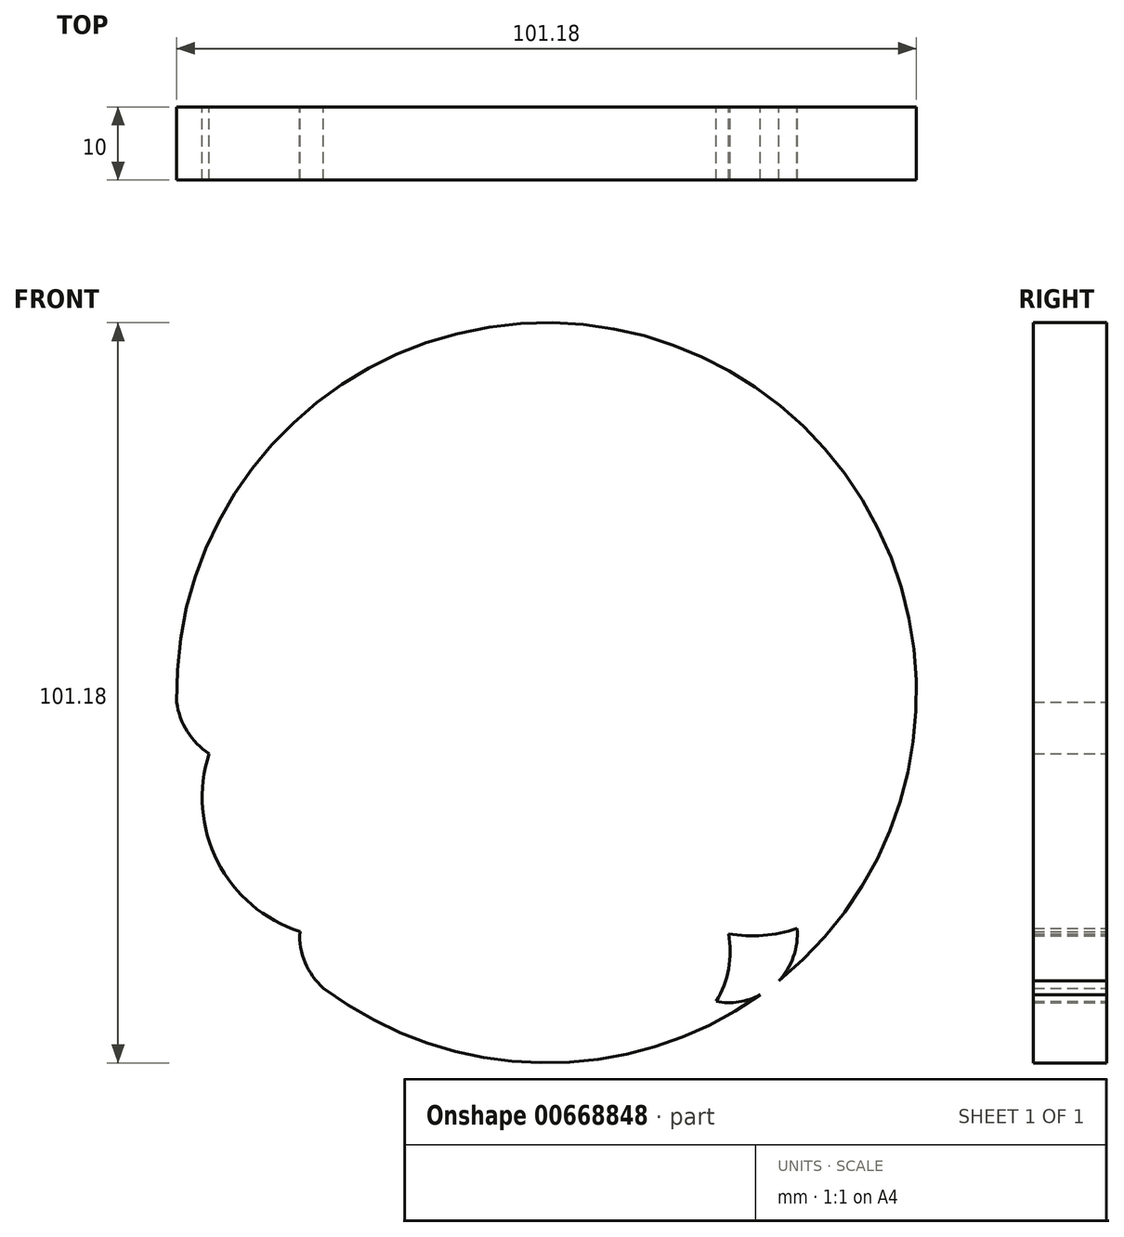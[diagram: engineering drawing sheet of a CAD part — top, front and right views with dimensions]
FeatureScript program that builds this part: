
annotation { "Feature Type Name" : "Feature", "Feature Type Description" : "" }
export const myFeature = defineFeature(function(context is Context, id is Id, definition is map)
    precondition{}
    {
        {
            var Q0;
            Q0=qCreatedBy(makeId("Front.planeOp"),FACE);
            var sketch = newSketch(context, id + "F0", { "sketchPlane" : qUnion([Q0])});
            skCircle(sketch, "E0", {"center": v(0, 0) * mm, "radius": 12.41 * mm});
            skCircle(sketch, "E1", {"center": v(0, 0) * mm, "radius": 50.59 * mm});
            skCircle(sketch, "E2", {"center": v(-26.62, 32.1) * mm, "radius": 8.89 * mm});
            skCircle(sketch, "E3", {"center": v(0, 41.3) * mm, "radius": 8.95 * mm});
            skCircle(sketch, "E4", {"center": v(27.2, 30.94) * mm, "radius": 9.28 * mm});
            skCircle(sketch, "E5", {"center": v(41.01, 0) * mm, "radius": 9.53 * mm});
            skCircle(sketch, "E6", {"center": v(-40.72, 0) * mm, "radius": 9.93 * mm});
            skCircle(sketch, "E7", {"center": v(0, -40.72) * mm, "radius": 9.22 * mm});
            skCircle(sketch, "E8", {"center": v(-24.32, -33.24) * mm, "radius": 9.43 * mm});
            skCircle(sketch, "E9", {"center": v(24.9, -32.95) * mm, "radius": 9.4 * mm});
            skLineSegment(sketch, "E10", {"start": v(0, 0) * mm, "end": v(0, 41.3) * mm});
            skLineSegment(sketch, "E11", {"start": v(0, 0) * mm, "end": v(27.2, 30.94) * mm});
            skLineSegment(sketch, "E12", {"start": v(0, 0) * mm, "end": v(41.01, 0) * mm});
            skLineSegment(sketch, "E13", {"start": v(0, 0) * mm, "end": v(24.9, -32.95) * mm});
            skLineSegment(sketch, "E14", {"start": v(0, 0) * mm, "end": v(0, -40.72) * mm});
            skLineSegment(sketch, "E15", {"start": v(0, 0) * mm, "end": v(-24.32, -33.24) * mm});
            skLineSegment(sketch, "E16", {"start": v(0, 0) * mm, "end": v(-40.72, 0) * mm});
            skLineSegment(sketch, "E17", {"start": v(0, 0) * mm, "end": v(-26.62, 32.1) * mm});
            skArc(sketch, "E18", {"start": v(-26.62, 32.1) * mm, "mid": v(-45.76, 21.36) * mm, "end": v(-40.72, 0) * mm});
            skArc(sketch, "E19", {"start": v(-40.72, 0) * mm, "mid": v(-45.1, -22.83) * mm, "end": v(-24.32, -33.24) * mm});
            skArc(sketch, "E20", {"start": v(-24.32, -33.24) * mm, "mid": v(-15.57, -48.07) * mm, "end": v(0, -40.72) * mm});
            skArc(sketch, "E21", {"start": v(0, -40.72) * mm, "mid": v(15.9, -47.9) * mm, "end": v(24.9, -32.95) * mm});
            skArc(sketch, "E22", {"start": v(24.9, -32.95) * mm, "mid": v(45.28, -22.5) * mm, "end": v(41.01, 0) * mm});
            skArc(sketch, "E23", {"start": v(41.01, 0) * mm, "mid": v(45.96, 20.76) * mm, "end": v(27.2, 30.94) * mm});
            skArc(sketch, "E24", {"start": v(27.2, 30.94) * mm, "mid": v(17.84, 47.26) * mm, "end": v(0, 41.3) * mm});
            skArc(sketch, "E25", {"start": v(0, 41.3) * mm, "mid": v(-17, 47.35) * mm, "end": v(-26.62, 32.1) * mm});
            skLineSegment(sketch, "E26", {"start": v(-29.07, 14.02) * mm, "end": v(-40.72, 0) * mm});
            skLineSegment(sketch, "E27", {"start": v(-29.07, 14.02) * mm, "end": v(-26.62, 32.1) * mm});
            skLineSegment(sketch, "E28", {"start": v(-12.28, 33.71) * mm, "end": v(-26.62, 32.1) * mm});
            skLineSegment(sketch, "E29", {"start": v(-12.28, 33.71) * mm, "end": v(0, 41.3) * mm});
            skLineSegment(sketch, "E30", {"start": v(0, 41.3) * mm, "end": v(12.56, 33.4) * mm});
            skLineSegment(sketch, "E31", {"start": v(12.56, 33.4) * mm, "end": v(27.2, 30.94) * mm});
            skLineSegment(sketch, "E32", {"start": v(27.2, 30.94) * mm, "end": v(29.94, 13.61) * mm});
            skLineSegment(sketch, "E33", {"start": v(29.94, 13.61) * mm, "end": v(41.01, 0) * mm});
            skLineSegment(sketch, "E34", {"start": v(41.01, 0) * mm, "end": v(28.11, -14.1) * mm});
            skLineSegment(sketch, "E35", {"start": v(28.11, -14.1) * mm, "end": v(24.9, -32.95) * mm});
            skLineSegment(sketch, "E36", {"start": v(24.9, -32.95) * mm, "end": v(11.99, -35.37) * mm});
            skLineSegment(sketch, "E37", {"start": v(11.99, -35.37) * mm, "end": v(0, -40.72) * mm});
            skLineSegment(sketch, "E38", {"start": v(0, -40.72) * mm, "end": v(-11.81, -35.85) * mm});
            skLineSegment(sketch, "E39", {"start": v(-11.81, -35.85) * mm, "end": v(-24.32, -33.24) * mm});
            skLineSegment(sketch, "E40", {"start": v(-24.32, -33.24) * mm, "end": v(-27.83, -14.3) * mm});
            skLineSegment(sketch, "E41", {"start": v(-27.83, -14.3) * mm, "end": v(-40.72, 0) * mm});
            skSolve(sketch);
        }
        {
            var Q0;
            {var subQ3=sQuery(id+"F0.wireOp",EDGE,"E11");var subQ10=sQuery(id+"F0.wireOp",EDGE,"E0");var subQ12=makeQuery(id+"F0.imprint","INTERSECT",VERTEX,{"derivedFrom":[subQ10,subQ3]});Q0=makeQuery(id+"F0.imprint","IMPRINT",FACE,{"disambiguationData":[TD([[makeQuery(id+"F0.imprint","IMPRINT",EDGE,{"disambiguationData":[TD([[subQ12,-1.0]])],"derivedFrom":subQ10}),-1.0]])]});}
            var Q1;
            {var subQ0=sQuery(id+"F0.wireOp",EDGE,"E10");var subQ1=sQuery(id+"F0.wireOp",EDGE,"E0");var subQ2=makeQuery(id+"F0.imprint","INTERSECT",VERTEX,{"derivedFrom":[subQ1,subQ0]});Q1=makeQuery(id+"F0.imprint","IMPRINT",FACE,{"disambiguationData":[TD([[makeQuery(id+"F0.imprint","IMPRINT",EDGE,{"disambiguationData":[TD([[subQ2,-1.0]])],"derivedFrom":subQ1}),-1.0]])]});}
            var Q2;
            {var subQ3=sQuery(id+"F0.wireOp",EDGE,"E2");var subQ5=sQuery(id+"F0.wireOp",EDGE,"E25");var subQ6=makeQuery(id+"F0.imprint","INTERSECT",VERTEX,{"derivedFrom":[subQ3,subQ5]});Q2=makeQuery(id+"F0.imprint","IMPRINT",FACE,{"disambiguationData":[TD([[makeQuery(id+"F0.imprint","IMPRINT",EDGE,{"disambiguationData":[TD([[subQ6,1.0]])],"derivedFrom":subQ3}),-1.0]])]});}
            var Q3;
            {var subQ0=sQuery(id+"F0.wireOp",EDGE,"E25");var subQ1=sQuery(id+"F0.wireOp",EDGE,"E3");var subQ2=makeQuery(id+"F0.imprint","INTERSECT",VERTEX,{"derivedFrom":[subQ1,subQ0]});Q3=makeQuery(id+"F0.imprint","IMPRINT",FACE,{"disambiguationData":[TD([[makeQuery(id+"F0.imprint","IMPRINT",EDGE,{"disambiguationData":[TD([[subQ2,-1.0]])],"derivedFrom":subQ1}),1.0]])]});}
            var Q4;
            {var subQ0=sQuery(id+"F0.wireOp",EDGE,"E25");var subQ1=sQuery(id+"F0.wireOp",EDGE,"E3");var subQ2=makeQuery(id+"F0.imprint","INTERSECT",VERTEX,{"derivedFrom":[subQ1,subQ0]});Q4=makeQuery(id+"F0.imprint","IMPRINT",FACE,{"disambiguationData":[TD([[makeQuery(id+"F0.imprint","IMPRINT",EDGE,{"disambiguationData":[TD([[subQ2,1.0]])],"derivedFrom":subQ1}),1.0]])]});}
            var Q5;
            {var subQ0=sQuery(id+"F0.wireOp",EDGE,"E24");var subQ1=sQuery(id+"F0.wireOp",EDGE,"E3");var subQ2=makeQuery(id+"F0.imprint","INTERSECT",VERTEX,{"derivedFrom":[subQ1,subQ0]});Q5=makeQuery(id+"F0.imprint","IMPRINT",FACE,{"disambiguationData":[TD([[makeQuery(id+"F0.imprint","IMPRINT",EDGE,{"disambiguationData":[TD([[subQ2,1.0]])],"derivedFrom":subQ1}),1.0]])]});}
            var Q6;
            {var subQ0=sQuery(id+"F0.wireOp",EDGE,"E10");var subQ1=sQuery(id+"F0.wireOp",EDGE,"E3");var subQ2=makeQuery(id+"F0.imprint","INTERSECT",VERTEX,{"derivedFrom":[subQ1,subQ0]});Q6=makeQuery(id+"F0.imprint","IMPRINT",FACE,{"disambiguationData":[TD([[makeQuery(id+"F0.imprint","IMPRINT",EDGE,{"disambiguationData":[TD([[subQ2,-1.0]])],"derivedFrom":subQ1}),1.0]])]});}
            var Q7;
            {var subQ0=sQuery(id+"F0.wireOp",EDGE,"E29");var subQ1=sQuery(id+"F0.wireOp",EDGE,"E3");var subQ2=makeQuery(id+"F0.imprint","INTERSECT",VERTEX,{"derivedFrom":[subQ1,subQ0]});Q7=makeQuery(id+"F0.imprint","IMPRINT",FACE,{"disambiguationData":[TD([[makeQuery(id+"F0.imprint","IMPRINT",EDGE,{"disambiguationData":[TD([[subQ2,-1.0]])],"derivedFrom":subQ1}),1.0]])]});}
            var Q8;
            {var subQ11=sQuery(id+"F0.wireOp",EDGE,"E6");var subQ12=sQuery(id+"F0.wireOp",EDGE,"E1");var subQ13=makeQuery(id+"F0.imprint","INTERSECT",VERTEX,{"disambiguationData":[OD(1.0)],"derivedFrom":[subQ12,subQ11]});Q8=makeQuery(id+"F0.imprint","IMPRINT",FACE,{"disambiguationData":[TD([[makeQuery(id+"F0.imprint","IMPRINT",EDGE,{"disambiguationData":[TD([[subQ13,1.0]])],"derivedFrom":subQ12}),1.0]])]});}
            var Q9;
            {var subQ5=sQuery(id+"F0.wireOp",EDGE,"E18");var subQ6=sQuery(id+"F0.wireOp",EDGE,"E2");var subQ7=makeQuery(id+"F0.imprint","INTERSECT",VERTEX,{"derivedFrom":[subQ6,subQ5]});Q9=makeQuery(id+"F0.imprint","IMPRINT",FACE,{"disambiguationData":[TD([[makeQuery(id+"F0.imprint","IMPRINT",EDGE,{"disambiguationData":[TD([[subQ7,-1.0]])],"derivedFrom":subQ6}),-1.0]])]});}
            var Q10;
            {var subQ0=sQuery(id+"F0.wireOp",EDGE,"E18");var subQ1=sQuery(id+"F0.wireOp",EDGE,"E2");var subQ2=makeQuery(id+"F0.imprint","INTERSECT",VERTEX,{"derivedFrom":[subQ1,subQ0]});Q10=makeQuery(id+"F0.imprint","IMPRINT",FACE,{"disambiguationData":[TD([[makeQuery(id+"F0.imprint","IMPRINT",EDGE,{"disambiguationData":[TD([[subQ2,-1.0]])],"derivedFrom":subQ1}),1.0]])]});}
            var Q11;
            {var subQ0=sQuery(id+"F0.wireOp",EDGE,"E25");var subQ1=sQuery(id+"F0.wireOp",EDGE,"E2");var subQ2=makeQuery(id+"F0.imprint","INTERSECT",VERTEX,{"derivedFrom":[subQ1,subQ0]});Q11=makeQuery(id+"F0.imprint","IMPRINT",FACE,{"disambiguationData":[TD([[makeQuery(id+"F0.imprint","IMPRINT",EDGE,{"disambiguationData":[TD([[subQ2,-1.0]])],"derivedFrom":subQ1}),1.0]])]});}
            var Q12;
            {var subQ0=sQuery(id+"F0.wireOp",EDGE,"E25");var subQ1=sQuery(id+"F0.wireOp",EDGE,"E2");var subQ2=makeQuery(id+"F0.imprint","INTERSECT",VERTEX,{"derivedFrom":[subQ1,subQ0]});Q12=makeQuery(id+"F0.imprint","IMPRINT",FACE,{"disambiguationData":[TD([[makeQuery(id+"F0.imprint","IMPRINT",EDGE,{"disambiguationData":[TD([[subQ2,1.0]])],"derivedFrom":subQ1}),1.0]])]});}
            var Q13;
            {var subQ0=sQuery(id+"F0.wireOp",EDGE,"E28");var subQ1=sQuery(id+"F0.wireOp",EDGE,"E2");var subQ2=makeQuery(id+"F0.imprint","INTERSECT",VERTEX,{"derivedFrom":[subQ1,subQ0]});Q13=makeQuery(id+"F0.imprint","IMPRINT",FACE,{"disambiguationData":[TD([[makeQuery(id+"F0.imprint","IMPRINT",EDGE,{"disambiguationData":[TD([[subQ2,1.0]])],"derivedFrom":subQ1}),1.0]])]});}
            var Q14;
            {var subQ0=sQuery(id+"F0.wireOp",EDGE,"E27");var subQ1=sQuery(id+"F0.wireOp",EDGE,"E2");var subQ2=makeQuery(id+"F0.imprint","INTERSECT",VERTEX,{"derivedFrom":[subQ1,subQ0]});Q14=makeQuery(id+"F0.imprint","IMPRINT",FACE,{"disambiguationData":[TD([[makeQuery(id+"F0.imprint","IMPRINT",EDGE,{"disambiguationData":[TD([[subQ2,-1.0]])],"derivedFrom":subQ1}),1.0]])]});}
            var Q15;
            {var subQ1=sQuery(id+"F0.wireOp",EDGE,"E0");var subQ10=sQuery(id+"F0.wireOp",EDGE,"E17");var subQ12=makeQuery(id+"F0.imprint","INTERSECT",VERTEX,{"derivedFrom":[subQ1,subQ10]});Q15=makeQuery(id+"F0.imprint","IMPRINT",FACE,{"disambiguationData":[TD([[makeQuery(id+"F0.imprint","IMPRINT",EDGE,{"disambiguationData":[TD([[subQ12,-1.0]])],"derivedFrom":subQ1}),-1.0]])]});}
            var Q16;
            {var subQ0=sQuery(id+"F0.wireOp",EDGE,"E16");var subQ1=sQuery(id+"F0.wireOp",EDGE,"E6");var subQ2=makeQuery(id+"F0.imprint","INTERSECT",VERTEX,{"derivedFrom":[subQ1,subQ0]});Q16=makeQuery(id+"F0.imprint","IMPRINT",FACE,{"disambiguationData":[TD([[makeQuery(id+"F0.imprint","IMPRINT",EDGE,{"disambiguationData":[TD([[subQ2,1.0]])],"derivedFrom":subQ1}),1.0]])]});}
            var Q17;
            {var subQ0=sQuery(id+"F0.wireOp",EDGE,"E26");var subQ1=sQuery(id+"F0.wireOp",EDGE,"E6");var subQ2=makeQuery(id+"F0.imprint","INTERSECT",VERTEX,{"derivedFrom":[subQ1,subQ0]});Q17=makeQuery(id+"F0.imprint","IMPRINT",FACE,{"disambiguationData":[TD([[makeQuery(id+"F0.imprint","IMPRINT",EDGE,{"disambiguationData":[TD([[subQ2,1.0]])],"derivedFrom":subQ1}),1.0]])]});}
            var Q18;
            {var subQ0=sQuery(id+"F0.wireOp",EDGE,"E26");var subQ1=sQuery(id+"F0.wireOp",EDGE,"E6");var subQ2=makeQuery(id+"F0.imprint","INTERSECT",VERTEX,{"derivedFrom":[subQ1,subQ0]});Q18=makeQuery(id+"F0.imprint","IMPRINT",FACE,{"disambiguationData":[TD([[makeQuery(id+"F0.imprint","IMPRINT",EDGE,{"disambiguationData":[TD([[subQ2,-1.0]])],"derivedFrom":subQ1}),1.0]])]});}
            var Q19;
            {var subQ3=sQuery(id+"F0.wireOp",EDGE,"E6");var subQ5=sQuery(id+"F0.wireOp",EDGE,"E1");var subQ7=makeQuery(id+"F0.imprint","INTERSECT",VERTEX,{"disambiguationData":[OD(0.0)],"derivedFrom":[subQ5,subQ3]});Q19=makeQuery(id+"F0.imprint","IMPRINT",FACE,{"disambiguationData":[TD([[makeQuery(id+"F0.imprint","IMPRINT",EDGE,{"disambiguationData":[TD([[subQ7,1.0]])],"derivedFrom":subQ5}),1.0]])]});}
            var Q20;
            {var subQ3=sQuery(id+"F0.wireOp",EDGE,"E6");var subQ5=sQuery(id+"F0.wireOp",EDGE,"E1");var subQ7=makeQuery(id+"F0.imprint","INTERSECT",VERTEX,{"disambiguationData":[OD(0.0)],"derivedFrom":[subQ5,subQ3]});Q20=makeQuery(id+"F0.imprint","IMPRINT",FACE,{"disambiguationData":[TD([[makeQuery(id+"F0.imprint","IMPRINT",EDGE,{"disambiguationData":[TD([[subQ7,1.0]])],"derivedFrom":subQ5}),1.0]])]});}
            var Q21;
            {var subQ0=sQuery(id+"F0.wireOp",EDGE,"E19");var subQ1=sQuery(id+"F0.wireOp",EDGE,"E6");var subQ2=makeQuery(id+"F0.imprint","INTERSECT",VERTEX,{"derivedFrom":[subQ1,subQ0]});Q21=makeQuery(id+"F0.imprint","IMPRINT",FACE,{"disambiguationData":[TD([[makeQuery(id+"F0.imprint","IMPRINT",EDGE,{"disambiguationData":[TD([[subQ2,-1.0]])],"derivedFrom":subQ1}),1.0]])]});}
            var Q22;
            {var subQ0=sQuery(id+"F0.wireOp",EDGE,"E6");var subQ1=sQuery(id+"F0.wireOp",EDGE,"E1");var subQ2=makeQuery(id+"F0.imprint","INTERSECT",VERTEX,{"disambiguationData":[OD(0.0)],"derivedFrom":[subQ1,subQ0]});Q22=makeQuery(id+"F0.imprint","IMPRINT",FACE,{"disambiguationData":[TD([[makeQuery(id+"F0.imprint","IMPRINT",EDGE,{"disambiguationData":[TD([[subQ2,-1.0]])],"derivedFrom":subQ1}),1.0]])]});}
            var Q23;
            {var subQ0=sQuery(id+"F0.wireOp",EDGE,"E19");var subQ1=sQuery(id+"F0.wireOp",EDGE,"E6");var subQ2=makeQuery(id+"F0.imprint","INTERSECT",VERTEX,{"derivedFrom":[subQ1,subQ0]});Q23=makeQuery(id+"F0.imprint","IMPRINT",FACE,{"disambiguationData":[TD([[makeQuery(id+"F0.imprint","IMPRINT",EDGE,{"disambiguationData":[TD([[subQ2,-1.0]])],"derivedFrom":subQ1}),-1.0]])]});}
            var Q24;
            {var subQ1=sQuery(id+"F0.wireOp",EDGE,"E0");var subQ7=sQuery(id+"F0.wireOp",EDGE,"E16");var subQ8=makeQuery(id+"F0.imprint","INTERSECT",VERTEX,{"derivedFrom":[subQ1,subQ7]});Q24=makeQuery(id+"F0.imprint","IMPRINT",FACE,{"disambiguationData":[TD([[makeQuery(id+"F0.imprint","IMPRINT",EDGE,{"disambiguationData":[TD([[subQ8,-1.0]])],"derivedFrom":subQ1}),-1.0]])]});}
            var Q25;
            {var subQ0=sQuery(id+"F0.wireOp",EDGE,"E40");var subQ1=sQuery(id+"F0.wireOp",EDGE,"E8");var subQ2=makeQuery(id+"F0.imprint","INTERSECT",VERTEX,{"derivedFrom":[subQ1,subQ0]});Q25=makeQuery(id+"F0.imprint","IMPRINT",FACE,{"disambiguationData":[TD([[makeQuery(id+"F0.imprint","IMPRINT",EDGE,{"disambiguationData":[TD([[subQ2,1.0]])],"derivedFrom":subQ1}),1.0]])]});}
            var Q26;
            {var subQ0=sQuery(id+"F0.wireOp",EDGE,"E40");var subQ1=sQuery(id+"F0.wireOp",EDGE,"E8");var subQ2=makeQuery(id+"F0.imprint","INTERSECT",VERTEX,{"derivedFrom":[subQ1,subQ0]});Q26=makeQuery(id+"F0.imprint","IMPRINT",FACE,{"disambiguationData":[TD([[makeQuery(id+"F0.imprint","IMPRINT",EDGE,{"disambiguationData":[TD([[subQ2,-1.0]])],"derivedFrom":subQ1}),1.0]])]});}
            var Q27;
            {var subQ3=sQuery(id+"F0.wireOp",EDGE,"E8");var subQ5=sQuery(id+"F0.wireOp",EDGE,"E1");var subQ6=makeQuery(id+"F0.imprint","INTERSECT",VERTEX,{"disambiguationData":[OD(0.0)],"derivedFrom":[subQ5,subQ3]});Q27=makeQuery(id+"F0.imprint","IMPRINT",FACE,{"disambiguationData":[TD([[makeQuery(id+"F0.imprint","IMPRINT",EDGE,{"disambiguationData":[TD([[subQ6,-1.0]])],"derivedFrom":subQ5}),1.0]])]});}
            var Q28;
            {var subQ0=sQuery(id+"F0.wireOp",EDGE,"E20");var subQ1=sQuery(id+"F0.wireOp",EDGE,"E8");var subQ2=makeQuery(id+"F0.imprint","INTERSECT",VERTEX,{"derivedFrom":[subQ1,subQ0]});Q28=makeQuery(id+"F0.imprint","IMPRINT",FACE,{"disambiguationData":[TD([[makeQuery(id+"F0.imprint","IMPRINT",EDGE,{"disambiguationData":[TD([[subQ2,-1.0]])],"derivedFrom":subQ1}),1.0]])]});}
            var Q29;
            {var subQ0=sQuery(id+"F0.wireOp",EDGE,"E15");var subQ1=sQuery(id+"F0.wireOp",EDGE,"E8");var subQ2=makeQuery(id+"F0.imprint","INTERSECT",VERTEX,{"derivedFrom":[subQ1,subQ0]});Q29=makeQuery(id+"F0.imprint","IMPRINT",FACE,{"disambiguationData":[TD([[makeQuery(id+"F0.imprint","IMPRINT",EDGE,{"disambiguationData":[TD([[subQ2,1.0]])],"derivedFrom":subQ1}),1.0]])]});}
            var Q30;
            {var subQ1=sQuery(id+"F0.wireOp",EDGE,"E0");var subQ5=sQuery(id+"F0.wireOp",EDGE,"E15");var subQ12=makeQuery(id+"F0.imprint","INTERSECT",VERTEX,{"derivedFrom":[subQ1,subQ5]});Q30=makeQuery(id+"F0.imprint","IMPRINT",FACE,{"disambiguationData":[TD([[makeQuery(id+"F0.imprint","IMPRINT",EDGE,{"disambiguationData":[TD([[subQ12,-1.0]])],"derivedFrom":subQ1}),-1.0]])]});}
            var Q31;
            {var subQ1=sQuery(id+"F0.wireOp",EDGE,"E7");var subQ7=sQuery(id+"F0.wireOp",EDGE,"E38");var subQ9=makeQuery(id+"F0.imprint","INTERSECT",VERTEX,{"derivedFrom":[subQ1,subQ7]});Q31=makeQuery(id+"F0.imprint","IMPRINT",FACE,{"disambiguationData":[TD([[makeQuery(id+"F0.imprint","IMPRINT",EDGE,{"disambiguationData":[TD([[subQ9,-1.0]])],"derivedFrom":subQ1}),-1.0]])]});}
            var Q32;
            {var subQ1=sQuery(id+"F0.wireOp",EDGE,"E1");var subQ5=sQuery(id+"F0.wireOp",EDGE,"E8");var subQ6=makeQuery(id+"F0.imprint","INTERSECT",VERTEX,{"disambiguationData":[OD(1.0)],"derivedFrom":[subQ1,subQ5]});Q32=makeQuery(id+"F0.imprint","IMPRINT",FACE,{"disambiguationData":[TD([[makeQuery(id+"F0.imprint","IMPRINT",EDGE,{"disambiguationData":[TD([[subQ6,-1.0]])],"derivedFrom":subQ1}),1.0]])]});}
            var Q33;
            {var subQ1=sQuery(id+"F0.wireOp",EDGE,"E0");var subQ7=sQuery(id+"F0.wireOp",EDGE,"E14");var subQ13=makeQuery(id+"F0.imprint","INTERSECT",VERTEX,{"derivedFrom":[subQ1,subQ7]});Q33=makeQuery(id+"F0.imprint","IMPRINT",FACE,{"disambiguationData":[TD([[makeQuery(id+"F0.imprint","IMPRINT",EDGE,{"disambiguationData":[TD([[subQ13,-1.0]])],"derivedFrom":subQ1}),-1.0]])]});}
            var Q34;
            {var subQ0=sQuery(id+"F0.wireOp",EDGE,"E37");var subQ6=sQuery(id+"F0.wireOp",EDGE,"E7");var subQ9=makeQuery(id+"F0.imprint","INTERSECT",VERTEX,{"derivedFrom":[subQ6,subQ0]});Q34=makeQuery(id+"F0.imprint","IMPRINT",FACE,{"disambiguationData":[TD([[makeQuery(id+"F0.imprint","IMPRINT",EDGE,{"disambiguationData":[TD([[subQ9,1.0]])],"derivedFrom":subQ6}),-1.0]])]});}
            var Q35;
            {var subQ0=sQuery(id+"F0.wireOp",EDGE,"E14");var subQ1=sQuery(id+"F0.wireOp",EDGE,"E7");var subQ2=makeQuery(id+"F0.imprint","INTERSECT",VERTEX,{"derivedFrom":[subQ1,subQ0]});Q35=makeQuery(id+"F0.imprint","IMPRINT",FACE,{"disambiguationData":[TD([[makeQuery(id+"F0.imprint","IMPRINT",EDGE,{"disambiguationData":[TD([[subQ2,1.0]])],"derivedFrom":subQ1}),1.0]])]});}
            var Q36;
            {var subQ0=sQuery(id+"F0.wireOp",EDGE,"E14");var subQ1=sQuery(id+"F0.wireOp",EDGE,"E7");var subQ2=makeQuery(id+"F0.imprint","INTERSECT",VERTEX,{"derivedFrom":[subQ1,subQ0]});Q36=makeQuery(id+"F0.imprint","IMPRINT",FACE,{"disambiguationData":[TD([[makeQuery(id+"F0.imprint","IMPRINT",EDGE,{"disambiguationData":[TD([[subQ2,-1.0]])],"derivedFrom":subQ1}),1.0]])]});}
            var Q37;
            {var subQ0=sQuery(id+"F0.wireOp",EDGE,"E38");var subQ1=sQuery(id+"F0.wireOp",EDGE,"E7");var subQ2=makeQuery(id+"F0.imprint","INTERSECT",VERTEX,{"derivedFrom":[subQ1,subQ0]});Q37=makeQuery(id+"F0.imprint","IMPRINT",FACE,{"disambiguationData":[TD([[makeQuery(id+"F0.imprint","IMPRINT",EDGE,{"disambiguationData":[TD([[subQ2,-1.0]])],"derivedFrom":subQ1}),1.0]])]});}
            var Q38;
            {var subQ0=sQuery(id+"F0.wireOp",EDGE,"E20");var subQ1=sQuery(id+"F0.wireOp",EDGE,"E7");var subQ2=makeQuery(id+"F0.imprint","INTERSECT",VERTEX,{"derivedFrom":[subQ1,subQ0]});Q38=makeQuery(id+"F0.imprint","IMPRINT",FACE,{"disambiguationData":[TD([[makeQuery(id+"F0.imprint","IMPRINT",EDGE,{"disambiguationData":[TD([[subQ2,-1.0]])],"derivedFrom":subQ1}),1.0]])]});}
            var Q39;
            {var subQ0=sQuery(id+"F0.wireOp",EDGE,"E37");var subQ1=sQuery(id+"F0.wireOp",EDGE,"E7");var subQ2=makeQuery(id+"F0.imprint","INTERSECT",VERTEX,{"derivedFrom":[subQ1,subQ0]});Q39=makeQuery(id+"F0.imprint","IMPRINT",FACE,{"disambiguationData":[TD([[makeQuery(id+"F0.imprint","IMPRINT",EDGE,{"disambiguationData":[TD([[subQ2,1.0]])],"derivedFrom":subQ1}),1.0]])]});}
            var Q40;
            {var subQ5=sQuery(id+"F0.wireOp",EDGE,"E12");var subQ10=sQuery(id+"F0.wireOp",EDGE,"E0");var subQ11=makeQuery(id+"F0.imprint","INTERSECT",VERTEX,{"derivedFrom":[subQ10,subQ5]});Q40=makeQuery(id+"F0.imprint","IMPRINT",FACE,{"disambiguationData":[TD([[makeQuery(id+"F0.imprint","IMPRINT",EDGE,{"disambiguationData":[TD([[subQ11,1.0]])],"derivedFrom":subQ10}),-1.0]])]});}
            var Q41;
            {var subQ1=sQuery(id+"F0.wireOp",EDGE,"E34");var subQ3=sQuery(id+"F0.wireOp",EDGE,"E5");var subQ4=makeQuery(id+"F0.imprint","INTERSECT",VERTEX,{"derivedFrom":[subQ3,subQ1]});Q41=makeQuery(id+"F0.imprint","IMPRINT",FACE,{"disambiguationData":[TD([[makeQuery(id+"F0.imprint","IMPRINT",EDGE,{"disambiguationData":[TD([[subQ4,-1.0]])],"derivedFrom":subQ3}),-1.0]])]});}
            var Q42;
            {var subQ0=sQuery(id+"F0.wireOp",EDGE,"E11");var subQ1=sQuery(id+"F0.wireOp",EDGE,"E0");var subQ2=makeQuery(id+"F0.imprint","INTERSECT",VERTEX,{"derivedFrom":[subQ1,subQ0]});Q42=makeQuery(id+"F0.imprint","IMPRINT",FACE,{"disambiguationData":[TD([[makeQuery(id+"F0.imprint","IMPRINT",EDGE,{"disambiguationData":[TD([[subQ2,1.0]])],"derivedFrom":subQ1}),-1.0]])]});}
            var Q43;
            {var subQ3=sQuery(id+"F0.wireOp",EDGE,"E3");var subQ7=sQuery(id+"F0.wireOp",EDGE,"E24");var subQ9=makeQuery(id+"F0.imprint","INTERSECT",VERTEX,{"derivedFrom":[subQ3,subQ7]});Q43=makeQuery(id+"F0.imprint","IMPRINT",FACE,{"disambiguationData":[TD([[makeQuery(id+"F0.imprint","IMPRINT",EDGE,{"disambiguationData":[TD([[subQ9,1.0]])],"derivedFrom":subQ3}),-1.0]])]});}
            var Q44;
            {var subQ0=sQuery(id+"F0.wireOp",EDGE,"E35");var subQ1=sQuery(id+"F0.wireOp",EDGE,"E9");var subQ2=makeQuery(id+"F0.imprint","INTERSECT",VERTEX,{"derivedFrom":[subQ1,subQ0]});Q44=makeQuery(id+"F0.imprint","IMPRINT",FACE,{"disambiguationData":[TD([[makeQuery(id+"F0.imprint","IMPRINT",EDGE,{"disambiguationData":[TD([[subQ2,-1.0]])],"derivedFrom":subQ1}),1.0]])]});}
            var Q45;
            {var subQ0=sQuery(id+"F0.wireOp",EDGE,"E13");var subQ1=sQuery(id+"F0.wireOp",EDGE,"E9");var subQ2=makeQuery(id+"F0.imprint","INTERSECT",VERTEX,{"derivedFrom":[subQ1,subQ0]});Q45=makeQuery(id+"F0.imprint","IMPRINT",FACE,{"disambiguationData":[TD([[makeQuery(id+"F0.imprint","IMPRINT",EDGE,{"disambiguationData":[TD([[subQ2,-1.0]])],"derivedFrom":subQ1}),1.0]])]});}
            var Q46;
            {var subQ0=sQuery(id+"F0.wireOp",EDGE,"E35");var subQ1=sQuery(id+"F0.wireOp",EDGE,"E9");var subQ2=makeQuery(id+"F0.imprint","INTERSECT",VERTEX,{"derivedFrom":[subQ1,subQ0]});Q46=makeQuery(id+"F0.imprint","IMPRINT",FACE,{"disambiguationData":[TD([[makeQuery(id+"F0.imprint","IMPRINT",EDGE,{"disambiguationData":[TD([[subQ2,1.0]])],"derivedFrom":subQ1}),1.0]])]});}
            var Q47;
            {var subQ0=sQuery(id+"F0.wireOp",EDGE,"E23");var subQ1=sQuery(id+"F0.wireOp",EDGE,"E5");var subQ2=makeQuery(id+"F0.imprint","INTERSECT",VERTEX,{"derivedFrom":[subQ1,subQ0]});Q47=makeQuery(id+"F0.imprint","IMPRINT",FACE,{"disambiguationData":[TD([[makeQuery(id+"F0.imprint","IMPRINT",EDGE,{"disambiguationData":[TD([[subQ2,1.0]])],"derivedFrom":subQ1}),1.0]])]});}
            var Q48;
            {var subQ0=sQuery(id+"F0.wireOp",EDGE,"E34");var subQ1=sQuery(id+"F0.wireOp",EDGE,"E5");var subQ2=makeQuery(id+"F0.imprint","INTERSECT",VERTEX,{"derivedFrom":[subQ1,subQ0]});Q48=makeQuery(id+"F0.imprint","IMPRINT",FACE,{"disambiguationData":[TD([[makeQuery(id+"F0.imprint","IMPRINT",EDGE,{"disambiguationData":[TD([[subQ2,-1.0]])],"derivedFrom":subQ1}),1.0]])]});}
            var Q49;
            {var subQ0=sQuery(id+"F0.wireOp",EDGE,"E33");var subQ1=sQuery(id+"F0.wireOp",EDGE,"E5");var subQ2=makeQuery(id+"F0.imprint","INTERSECT",VERTEX,{"derivedFrom":[subQ1,subQ0]});Q49=makeQuery(id+"F0.imprint","IMPRINT",FACE,{"disambiguationData":[TD([[makeQuery(id+"F0.imprint","IMPRINT",EDGE,{"disambiguationData":[TD([[subQ2,1.0]])],"derivedFrom":subQ1}),1.0]])]});}
            var Q50;
            {var subQ1=sQuery(id+"F0.wireOp",EDGE,"E32");var subQ3=sQuery(id+"F0.wireOp",EDGE,"E4");var subQ4=makeQuery(id+"F0.imprint","INTERSECT",VERTEX,{"derivedFrom":[subQ3,subQ1]});Q50=makeQuery(id+"F0.imprint","IMPRINT",FACE,{"disambiguationData":[TD([[makeQuery(id+"F0.imprint","IMPRINT",EDGE,{"disambiguationData":[TD([[subQ4,-1.0]])],"derivedFrom":subQ3}),-1.0]])]});}
            var Q51;
            {var subQ0=sQuery(id+"F0.wireOp",EDGE,"E36");var subQ1=sQuery(id+"F0.wireOp",EDGE,"E9");var subQ2=makeQuery(id+"F0.imprint","INTERSECT",VERTEX,{"derivedFrom":[subQ1,subQ0]});Q51=makeQuery(id+"F0.imprint","IMPRINT",FACE,{"disambiguationData":[TD([[makeQuery(id+"F0.imprint","IMPRINT",EDGE,{"disambiguationData":[TD([[subQ2,-1.0]])],"derivedFrom":subQ1}),1.0]])]});}
            var Q52;
            {var subQ3=sQuery(id+"F0.wireOp",EDGE,"E9");var subQ5=sQuery(id+"F0.wireOp",EDGE,"E1");var subQ8=makeQuery(id+"F0.imprint","INTERSECT",VERTEX,{"disambiguationData":[OD(0.0)],"derivedFrom":[subQ5,subQ3]});Q52=makeQuery(id+"F0.imprint","IMPRINT",FACE,{"disambiguationData":[TD([[makeQuery(id+"F0.imprint","IMPRINT",EDGE,{"disambiguationData":[TD([[subQ8,-1.0]])],"derivedFrom":subQ5}),1.0]])]});}
            var Q53;
            {var subQ0=sQuery(id+"F0.wireOp",EDGE,"E33");var subQ1=sQuery(id+"F0.wireOp",EDGE,"E5");var subQ2=makeQuery(id+"F0.imprint","INTERSECT",VERTEX,{"derivedFrom":[subQ1,subQ0]});Q53=makeQuery(id+"F0.imprint","IMPRINT",FACE,{"disambiguationData":[TD([[makeQuery(id+"F0.imprint","IMPRINT",EDGE,{"disambiguationData":[TD([[subQ2,-1.0]])],"derivedFrom":subQ1}),1.0]])]});}
            var Q54;
            {var subQ0=sQuery(id+"F0.wireOp",EDGE,"E12");var subQ1=sQuery(id+"F0.wireOp",EDGE,"E5");var subQ2=makeQuery(id+"F0.imprint","INTERSECT",VERTEX,{"derivedFrom":[subQ1,subQ0]});Q54=makeQuery(id+"F0.imprint","IMPRINT",FACE,{"disambiguationData":[TD([[makeQuery(id+"F0.imprint","IMPRINT",EDGE,{"disambiguationData":[TD([[subQ2,-1.0]])],"derivedFrom":subQ1}),1.0]])]});}
            var Q55;
            {var subQ0=sQuery(id+"F0.wireOp",EDGE,"E31");var subQ1=sQuery(id+"F0.wireOp",EDGE,"E4");var subQ2=makeQuery(id+"F0.imprint","INTERSECT",VERTEX,{"derivedFrom":[subQ1,subQ0]});Q55=makeQuery(id+"F0.imprint","IMPRINT",FACE,{"disambiguationData":[TD([[makeQuery(id+"F0.imprint","IMPRINT",EDGE,{"disambiguationData":[TD([[subQ2,1.0]])],"derivedFrom":subQ1}),1.0]])]});}
            var Q56;
            {var subQ0=sQuery(id+"F0.wireOp",EDGE,"E24");var subQ1=sQuery(id+"F0.wireOp",EDGE,"E4");var subQ2=makeQuery(id+"F0.imprint","INTERSECT",VERTEX,{"derivedFrom":[subQ1,subQ0]});Q56=makeQuery(id+"F0.imprint","IMPRINT",FACE,{"disambiguationData":[TD([[makeQuery(id+"F0.imprint","IMPRINT",EDGE,{"disambiguationData":[TD([[subQ2,1.0]])],"derivedFrom":subQ1}),1.0]])]});}
            var Q57;
            {var subQ0=sQuery(id+"F0.wireOp",EDGE,"E32");var subQ1=sQuery(id+"F0.wireOp",EDGE,"E4");var subQ2=makeQuery(id+"F0.imprint","INTERSECT",VERTEX,{"derivedFrom":[subQ1,subQ0]});Q57=makeQuery(id+"F0.imprint","IMPRINT",FACE,{"disambiguationData":[TD([[makeQuery(id+"F0.imprint","IMPRINT",EDGE,{"disambiguationData":[TD([[subQ2,-1.0]])],"derivedFrom":subQ1}),1.0]])]});}
            var Q58;
            {var subQ0=sQuery(id+"F0.wireOp",EDGE,"E11");var subQ1=sQuery(id+"F0.wireOp",EDGE,"E4");var subQ2=makeQuery(id+"F0.imprint","INTERSECT",VERTEX,{"derivedFrom":[subQ1,subQ0]});Q58=makeQuery(id+"F0.imprint","IMPRINT",FACE,{"disambiguationData":[TD([[makeQuery(id+"F0.imprint","IMPRINT",EDGE,{"disambiguationData":[TD([[subQ2,-1.0]])],"derivedFrom":subQ1}),1.0]])]});}
            var Q59;
            {var subQ0=sQuery(id+"F0.wireOp",EDGE,"E31");var subQ1=sQuery(id+"F0.wireOp",EDGE,"E4");var subQ2=makeQuery(id+"F0.imprint","INTERSECT",VERTEX,{"derivedFrom":[subQ1,subQ0]});Q59=makeQuery(id+"F0.imprint","IMPRINT",FACE,{"disambiguationData":[TD([[makeQuery(id+"F0.imprint","IMPRINT",EDGE,{"disambiguationData":[TD([[subQ2,-1.0]])],"derivedFrom":subQ1}),1.0]])]});}
            var Q60;
            {var subQ0=sQuery(id+"F0.wireOp",EDGE,"E11");var subQ1=sQuery(id+"F0.wireOp",EDGE,"E0");var subQ2=makeQuery(id+"F0.imprint","INTERSECT",VERTEX,{"derivedFrom":[subQ1,subQ0]});Q60=makeQuery(id+"F0.imprint","IMPRINT",FACE,{"disambiguationData":[TD([[makeQuery(id+"F0.imprint","IMPRINT",EDGE,{"disambiguationData":[TD([[subQ2,-1.0]])],"derivedFrom":subQ1}),1.0]])]});}
            var Q61;
            {var subQ0=sQuery(id+"F0.wireOp",EDGE,"E10");var subQ1=sQuery(id+"F0.wireOp",EDGE,"E0");var subQ2=makeQuery(id+"F0.imprint","INTERSECT",VERTEX,{"derivedFrom":[subQ1,subQ0]});Q61=makeQuery(id+"F0.imprint","IMPRINT",FACE,{"disambiguationData":[TD([[makeQuery(id+"F0.imprint","IMPRINT",EDGE,{"disambiguationData":[TD([[subQ2,-1.0]])],"derivedFrom":subQ1}),1.0]])]});}
            var Q62;
            {var subQ0=sQuery(id+"F0.wireOp",EDGE,"E17");var subQ1=sQuery(id+"F0.wireOp",EDGE,"E0");var subQ2=makeQuery(id+"F0.imprint","INTERSECT",VERTEX,{"derivedFrom":[subQ1,subQ0]});Q62=makeQuery(id+"F0.imprint","IMPRINT",FACE,{"disambiguationData":[TD([[makeQuery(id+"F0.imprint","IMPRINT",EDGE,{"disambiguationData":[TD([[subQ2,-1.0]])],"derivedFrom":subQ1}),1.0]])]});}
            var Q63;
            {var subQ0=sQuery(id+"F0.wireOp",EDGE,"E16");var subQ1=sQuery(id+"F0.wireOp",EDGE,"E0");var subQ2=makeQuery(id+"F0.imprint","INTERSECT",VERTEX,{"derivedFrom":[subQ1,subQ0]});Q63=makeQuery(id+"F0.imprint","IMPRINT",FACE,{"disambiguationData":[TD([[makeQuery(id+"F0.imprint","IMPRINT",EDGE,{"disambiguationData":[TD([[subQ2,-1.0]])],"derivedFrom":subQ1}),1.0]])]});}
            var Q64;
            {var subQ0=sQuery(id+"F0.wireOp",EDGE,"E15");var subQ1=sQuery(id+"F0.wireOp",EDGE,"E0");var subQ2=makeQuery(id+"F0.imprint","INTERSECT",VERTEX,{"derivedFrom":[subQ1,subQ0]});Q64=makeQuery(id+"F0.imprint","IMPRINT",FACE,{"disambiguationData":[TD([[makeQuery(id+"F0.imprint","IMPRINT",EDGE,{"disambiguationData":[TD([[subQ2,-1.0]])],"derivedFrom":subQ1}),1.0]])]});}
            var Q65;
            {var subQ0=sQuery(id+"F0.wireOp",EDGE,"E14");var subQ1=sQuery(id+"F0.wireOp",EDGE,"E0");var subQ2=makeQuery(id+"F0.imprint","INTERSECT",VERTEX,{"derivedFrom":[subQ1,subQ0]});Q65=makeQuery(id+"F0.imprint","IMPRINT",FACE,{"disambiguationData":[TD([[makeQuery(id+"F0.imprint","IMPRINT",EDGE,{"disambiguationData":[TD([[subQ2,-1.0]])],"derivedFrom":subQ1}),1.0]])]});}
            var Q66;
            {var subQ0=sQuery(id+"F0.wireOp",EDGE,"E12");var subQ1=sQuery(id+"F0.wireOp",EDGE,"E0");var subQ2=makeQuery(id+"F0.imprint","INTERSECT",VERTEX,{"derivedFrom":[subQ1,subQ0]});Q66=makeQuery(id+"F0.imprint","IMPRINT",FACE,{"disambiguationData":[TD([[makeQuery(id+"F0.imprint","IMPRINT",EDGE,{"disambiguationData":[TD([[subQ2,1.0]])],"derivedFrom":subQ1}),1.0]])]});}
            var Q67;
            {var subQ0=sQuery(id+"F0.wireOp",EDGE,"E11");var subQ1=sQuery(id+"F0.wireOp",EDGE,"E0");var subQ2=makeQuery(id+"F0.imprint","INTERSECT",VERTEX,{"derivedFrom":[subQ1,subQ0]});Q67=makeQuery(id+"F0.imprint","IMPRINT",FACE,{"disambiguationData":[TD([[makeQuery(id+"F0.imprint","IMPRINT",EDGE,{"disambiguationData":[TD([[subQ2,1.0]])],"derivedFrom":subQ1}),1.0]])]});}
            var Q68;
            Q68 = qSketchRegion(id + "F2", true);
            extrude(context, id + "F1", {"entities" : qUnion([Q0, Q1, Q2, Q3, Q4, Q5, Q6, Q7, Q8, Q9, Q10, Q11, Q12, Q13, Q14, Q15, Q16, Q17, Q18, Q19, Q20, Q21, Q22, Q23, Q24, Q25, Q26, Q27, Q28, Q29, Q30, Q31, Q32, Q33, Q34, Q35, Q36, Q37, Q38, Q39, Q40, Q41, Q42, Q43, Q44, Q45, Q46, Q47, Q48, Q49, Q50, Q51, Q52, Q53, Q54, Q55, Q56, Q57, Q58, Q59, Q60, Q61, Q62, Q63, Q64, Q65, Q66, Q67, Q68]), "depth" : 10 * mm, "offsetDistance" : 25 * mm});
        }
    });
